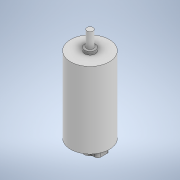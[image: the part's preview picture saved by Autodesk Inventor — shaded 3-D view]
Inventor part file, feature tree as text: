
AUTODESK INVENTOR PART (.ipt)
format: ipt  version: 2020 (Build 240168000, 168)  size: 140,800 bytes
history: native  units: mm
features: extrude x5, sketch x5, other x1, fillet x1
ambient origin geometry x8: Origin, YZ Plane, XZ Plane, XY Plane, X Axis, Y Axis, Z Axis, Center Point
bodies: Body1 (feature_tree)
feature tree (12):
  other  "Bryła1"
  extrude  "Wyciągnięcie proste1"  Depth=25.0mm
  extrude  "Wyciągnięcie proste2"  Depth=56.0mm TaperAngle=0.0deg
  extrude  "Wyciągnięcie proste3"  Depth=4.0mm
  extrude  "Wyciągnięcie proste4"  Depth=12.0mm TaperAngle=0.0deg
  extrude  "Wyciągnięcie proste5"  Depth=7.0mm
  fillet  "Zaokrąglenie1"  Radius=2.0mm
  sketch  "Szkic1"
  sketch  "Szkic2"
  sketch  "Szkic3"
  sketch  "Szkic4"
  sketch  "Szkic5"
